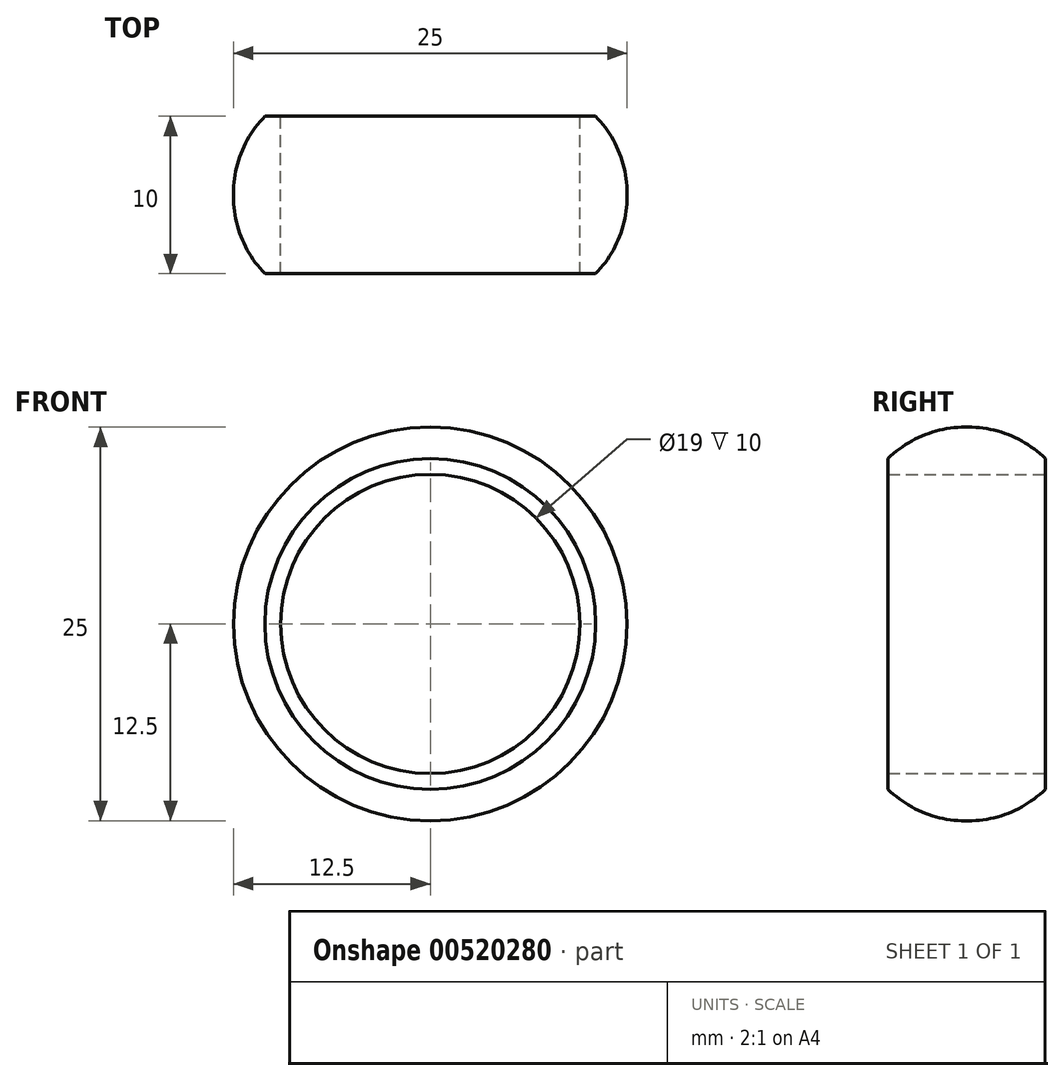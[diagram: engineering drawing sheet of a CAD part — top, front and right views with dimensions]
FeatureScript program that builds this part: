
annotation { "Feature Type Name" : "Feature", "Feature Type Description" : "" }
export const myFeature = defineFeature(function(context is Context, id is Id, definition is map)
    precondition{}
    {
        {
            var Q0;
            Q0=qCreatedBy(makeId("Front.planeOp"),FACE);
            var sketch = newSketch(context, id + "F0", { "sketchPlane" : qUnion([Q0])});
            skCircle(sketch, "E0", {"center": v(0, 0) * mm, "radius": 9.5 * mm});
            skCircle(sketch, "E1", {"center": v(0, 0) * mm, "radius": 12.5 * mm});
            skCircle(sketch, "E2", {"center": v(0, 0) * mm, "radius": 10.5 * mm});
            skSolve(sketch);
        }
        {
            var Q0;
            Q0=makeQuery(id+"F0.imprint","IMPRINT",FACE,{"disambiguationData":[TD([[makeQuery(id+"F0.imprint","IMPRINT",EDGE,{"derivedFrom":sQuery(id+"F0.wireOp",EDGE,"E1")}),1.0]])]});
            extrude(context, id + "F1", {"entities" : qUnion([Q0]), "depth" : 10 * mm, "offsetDistance" : 25 * mm});
        }
        {
            var Q0;
            Q0=makeQuery(id+"F1.opExtrude","SWEPT_FACE",FACE,{"disambiguationData":[OSD([sQuery(id+"F0.wireOp",EDGE,"E1")])]});
            var Q1;
            Q1=makeQuery(id+"F1.opExtrude","CAP_EDGE",EDGE,{"disambiguationData":[OSD([sQuery(id+"F0.wireOp",EDGE,"E1")])],"isStart":true});
            fillet(context, id + "F2", {"entities" : qUnion([Q0, Q1]), "radius" : 7 * mm, "tangentPropagation" : true, "allowEdgeOverflow" : false});
        }
        {
            var Q0;
            Q0=makeQuery(id+"F0.imprint","IMPRINT",FACE,{"disambiguationData":[TD([[makeQuery(id+"F0.imprint","IMPRINT",EDGE,{"derivedFrom":sQuery(id+"F0.wireOp",EDGE,"E0")}),-1.0]])]});
            extrude(context, id + "F3", {"entities" : qUnion([Q0]), "operationType" : NewBodyOperationType.ADD, "depth" : 10 * mm, "offsetDistance" : 25 * mm});
        }
    });
